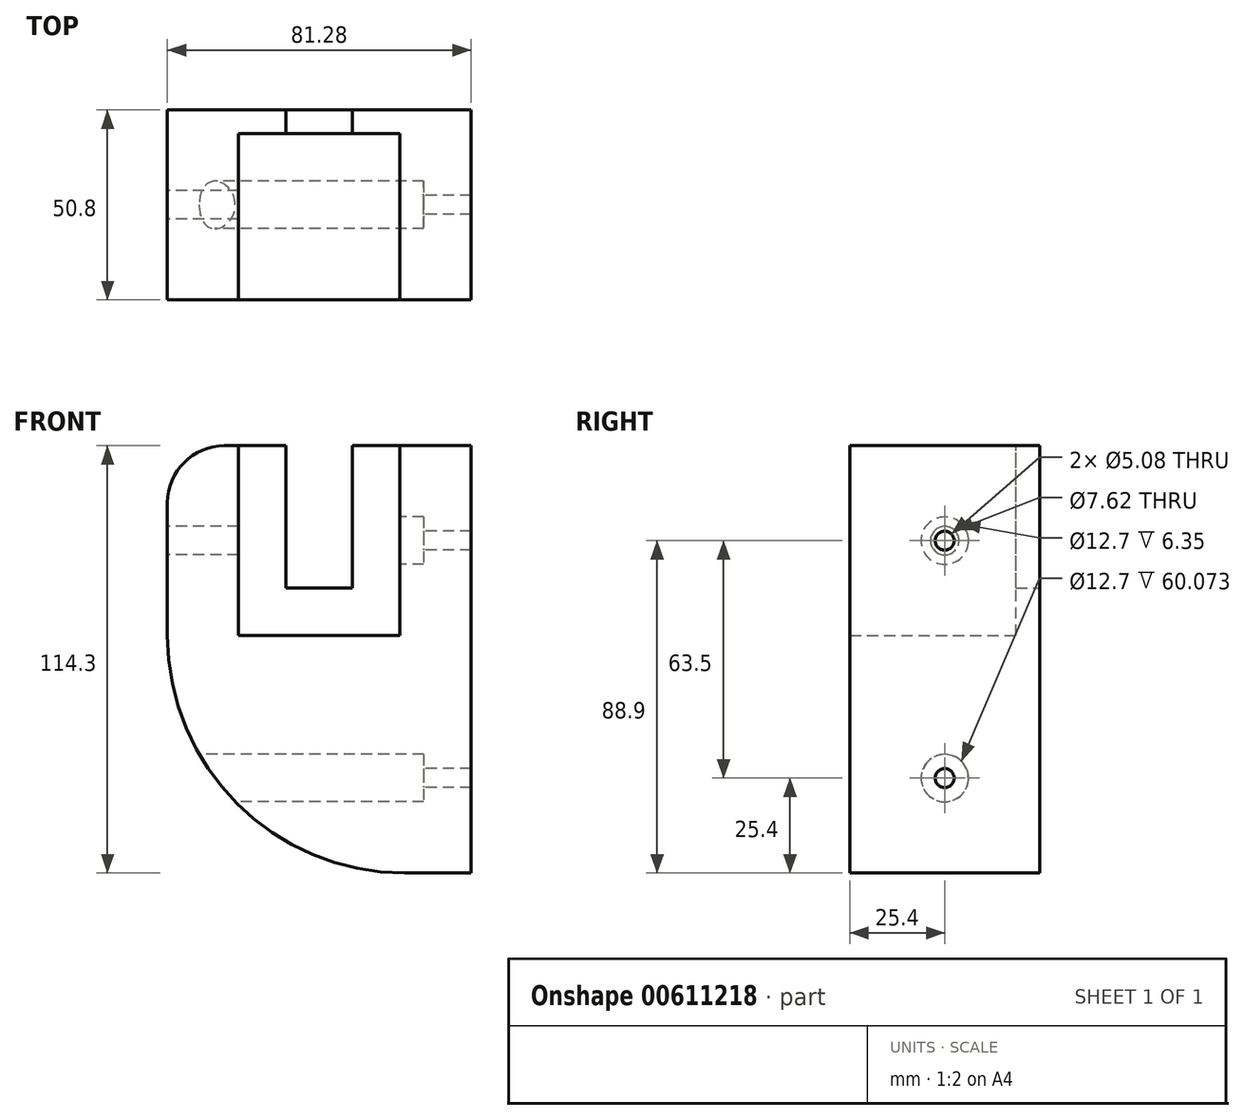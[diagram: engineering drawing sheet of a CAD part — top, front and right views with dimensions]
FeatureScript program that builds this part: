
annotation { "Feature Type Name" : "Feature", "Feature Type Description" : "" }
export const myFeature = defineFeature(function(context is Context, id is Id, definition is map)
    precondition{}
    {
        {
            var Q0;
            Q0=qCreatedBy(makeId("Front.planeOp"),FACE);
            var sketch = newSketch(context, id + "F0", { "sketchPlane" : qUnion([Q0])});
            skLineSegment(sketch, "E0", {"start": v(0, 0) * mm, "end": v(0, 50.8) * mm});
            skLineSegment(sketch, "E1", {"start": v(0, 50.8) * mm, "end": v(19.05, 50.8) * mm});
            skLineSegment(sketch, "E2", {"start": v(19.05, 50.8) * mm, "end": v(19.05, -63.5) * mm});
            skLineSegment(sketch, "E3", {"start": v(-43.18, 50.8) * mm, "end": v(-43.18, 0) * mm});
            skLineSegment(sketch, "E4", {"start": v(-43.18, 0) * mm, "end": v(0, 0) * mm});
            skLineSegment(sketch, "E5", {"start": v(1.27, -63.5) * mm, "end": v(19.05, -63.5) * mm});
            skLineSegment(sketch, "E6", {"start": v(-43.18, 50.8) * mm, "end": v(-46.99, 50.8) * mm});
            skLineSegment(sketch, "E7", {"start": v(-62.23, 35.56) * mm, "end": v(-62.23, 0) * mm});
            skPoint(sketch, "E8.visualSharp", {"position": v(-62.23, -63.5) * mm});
            skArc(sketch, "E8.filletArc", {"start": v(-62.23, 0) * mm, "mid": v(-43.63, -44.9) * mm, "end": v(1.27, -63.5) * mm});
            skPoint(sketch, "E9.visualSharp", {"position": v(-62.23, 50.8) * mm});
            skArc(sketch, "E9.filletArc", {"start": v(-46.99, 50.8) * mm, "mid": v(-57.77, 46.34) * mm, "end": v(-62.23, 35.56) * mm});
            skLineSegment(sketch, "E10", {"start": v(-43.18, 50.8) * mm, "end": v(-30.48, 50.8) * mm});
            skLineSegment(sketch, "E11", {"start": v(-30.48, 50.8) * mm, "end": v(-30.48, 12.7) * mm});
            skLineSegment(sketch, "E12", {"start": v(-30.48, 12.7) * mm, "end": v(-12.7, 12.7) * mm});
            skLineSegment(sketch, "E13", {"start": v(-12.7, 12.7) * mm, "end": v(-12.7, 50.8) * mm});
            skLineSegment(sketch, "E14", {"start": v(0, 50.8) * mm, "end": v(-12.7, 50.8) * mm});
            skSolve(sketch);
        }
        {
            var Q0;
            Q0=makeQuery(id+"F0.imprint","IMPRINT",FACE,{"disambiguationData":[TD([[makeQuery(id+"F0.imprint","IMPRINT",EDGE,{"derivedFrom":sQuery(id+"F0.wireOp",EDGE,"E0")}),-1.0]])]});
            extrude(context, id + "F1", {"entities" : qUnion([Q0]), "depth" : 50.8 * mm, "offsetDistance" : 25.4 * mm});
        }
        {
            var Q0;
            Q0 = qSketchRegion(id + "F0", true);
            extrude(context, id + "F2", {"entities" : qUnion([Q0]), "operationType" : NewBodyOperationType.ADD, "depth" : 6.35 * mm, "offsetDistance" : 25.4 * mm});
        }
        {
            var Q0;
            Q0=makeQuery(id+"F1.opExtrude","SWEPT_FACE",FACE,{"disambiguationData":[OSD([sQuery(id+"F0.wireOp",EDGE,"E7")])]});
            var sketch = newSketch(context, id + "F3", { "sketchPlane" : qUnion([Q0])});
            skCircle(sketch, "E15", {"center": v(25.4, 25.4) * mm, "radius": 3.81 * mm});
            skPoint(sketch, "E15.centerSnap0", {"position": v(25.4, 0) * mm});
            skSolve(sketch);
        }
        {
            var Q0;
            Q0=makeQuery(id+"F3.imprint","IMPRINT",FACE,{"disambiguationData":[TD([[makeQuery(id+"F3.imprint","IMPRINT",EDGE,{"derivedFrom":sQuery(id+"F3.wireOp",EDGE,"E15")}),1.0]])]});
            extrude(context, id + "F4", {"entities" : qUnion([Q0]), "operationType" : NewBodyOperationType.REMOVE, "endBound" : BoundingType.UP_TO_NEXT, "oppositeDirection" : true, "depth" : 25.4 * mm, "offsetDistance" : 25.4 * mm});
        }
        {
            var Q0;
            Q0=makeQuery(id+"F1.opExtrude","SWEPT_FACE",FACE,{"disambiguationData":[OSD([sQuery(id+"F0.wireOp",EDGE,"E0")])]});
            var sketch = newSketch(context, id + "F5", { "sketchPlane" : qUnion([Q0])});
            skCircle(sketch, "E16", {"center": v(25.4, 25.4) * mm, "radius": 6.35 * mm});
            skSolve(sketch);
        }
        {
            var Q0;
            Q0 = qSketchRegion(id + "F5", true);
            extrude(context, id + "F6", {"entities" : qUnion([Q0]), "operationType" : NewBodyOperationType.REMOVE, "oppositeDirection" : true, "depth" : 6.35 * mm, "offsetDistance" : 25.4 * mm});
        }
        {
            var Q0;
            Q0=makeQuery(id+"F6.boolean.opBoolean","COPY",FACE,{"derivedFrom":makeQuery(id+"F6.opExtrude","CAP_FACE",FACE,{"disambiguationData":[OSD([sQuery(id+"F5.wireOp",EDGE,"E16")])],"isStart":false})});
            var sketch = newSketch(context, id + "F7", { "sketchPlane" : qUnion([Q0])});
            skCircle(sketch, "E17", {"center": v(25.4, 25.4) * mm, "radius": 2.54 * mm});
            skSolve(sketch);
        }
        {
            var Q0;
            Q0 = qSketchRegion(id + "F7", true);
            extrude(context, id + "F8", {"entities" : qUnion([Q0]), "operationType" : NewBodyOperationType.REMOVE, "endBound" : BoundingType.THROUGH_ALL, "oppositeDirection" : true, "depth" : 25.4 * mm, "offsetDistance" : 25.4 * mm});
        }
        {
            var Q0;
            Q0=makeQuery(id+"F1.opExtrude","SWEPT_FACE",FACE,{"disambiguationData":[OSD([sQuery(id+"F0.wireOp",EDGE,"E7")])]});
            var sketch = newSketch(context, id + "F9", { "sketchPlane" : qUnion([Q0])});
            skCircle(sketch, "E18", {"center": v(25.4, -38.1) * mm, "radius": 2.54 * mm});
            skPoint(sketch, "E18.centerSnap0", {"position": v(25.4, 0) * mm});
            skCircle(sketch, "E19", {"center": v(25.4, -38.1) * mm, "radius": 6.35 * mm});
            skSolve(sketch);
        }
        {
            var Q0;
            Q0=makeQuery(id+"F9.imprint","IMPRINT",FACE,{"disambiguationData":[TD([[makeQuery(id+"F9.imprint","IMPRINT",EDGE,{"derivedFrom":sQuery(id+"F9.wireOp",EDGE,"E18")}),1.0]])]});
            extrude(context, id + "F10", {"entities" : qUnion([Q0]), "operationType" : NewBodyOperationType.REMOVE, "endBound" : BoundingType.THROUGH_ALL, "oppositeDirection" : true, "depth" : 25.4 * mm, "offsetDistance" : 25.4 * mm});
        }
        {
            var Q0;
            Q0 = qSketchRegion(id + "F9", true);
            extrude(context, id + "F11", {"entities" : qUnion([Q0]), "operationType" : NewBodyOperationType.REMOVE, "oppositeDirection" : true, "depth" : 68.58 * mm, "offsetDistance" : 25.4 * mm});
        }
    });
